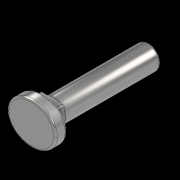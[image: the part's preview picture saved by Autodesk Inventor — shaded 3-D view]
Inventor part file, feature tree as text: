
AUTODESK INVENTOR PART (.ipt)
format: ipt  version: 2022.2 (Build 262287010, 287A)  size: 240,128 bytes
history: native  units: mm
features: extrude x3, sketch x3, fillet x2, thread x1
ambient origin geometry x8: Origin, YZ Plane, XZ Plane, XY Plane, X Axis, Y Axis, Z Axis, Center Point
bodies: Solid1 (feature_tree)
feature tree (9):
  extrude  "Extrusion1"  Depth=4.8mm
  extrude  "Extrusion2"  Depth=25.5mm
  extrude  "Extrusion3"  Depth=25.5mm TaperAngle=0.0deg
  fillet  "Fillet1"  Radius=5.45mm
  fillet  "Fillet2"  Radius=6.4mm
  thread  "Thread1"  [1 undecoded]
  sketch  "Sketch1"  dims[d0=6.2mm d1=4.8mm]
  sketch  "Sketch2"  dims[d2=25.5mm d3=0.0mm d4=6.35mm]
  sketch  "Sketch3"  dims[d5=6.35mm d6=2.5mm d7=0.0mm d8=5.45mm d9=6.4mm d10=3.0mm d11=0.0mm d12=0.5mm d13=0.5mm d14=25.5mm d15=0.0mm]
note: 1 required parameter value undecoded (feature->parameter linkage not recoverable at this tier; creation-order binding heuristic only, values carry confidence <= 0.55)
